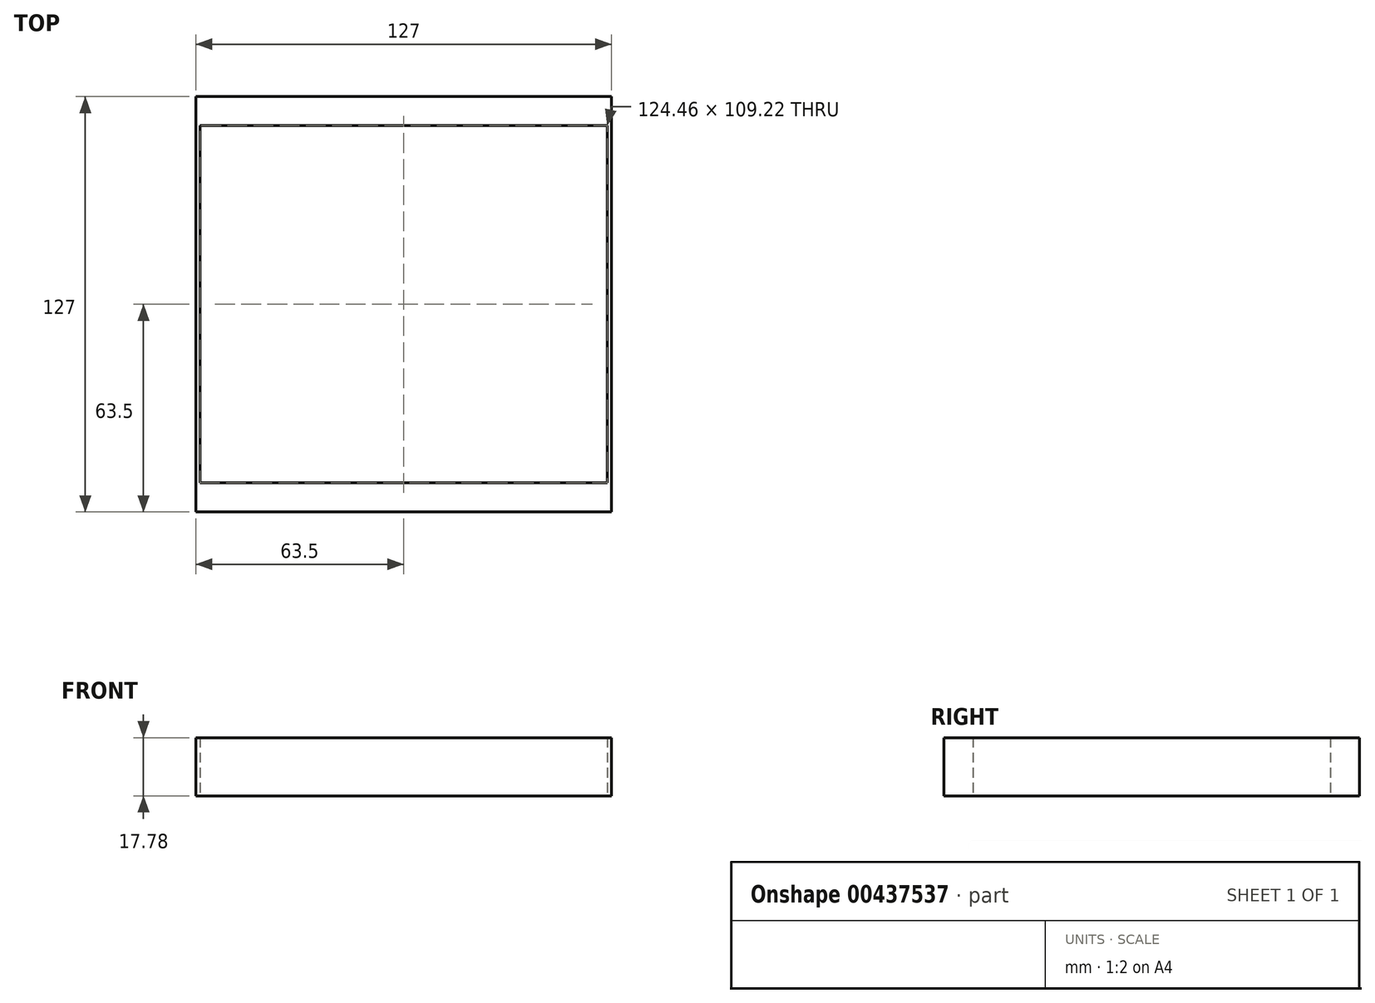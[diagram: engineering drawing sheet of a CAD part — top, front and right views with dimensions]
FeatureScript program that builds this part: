
annotation { "Feature Type Name" : "Feature", "Feature Type Description" : "" }
export const myFeature = defineFeature(function(context is Context, id is Id, definition is map)
    precondition{}
    {
        {
            var Q0;
            Q0=qCreatedBy(makeId("Top.planeOp"),FACE);
            var sketch = newSketch(context, id + "F0", { "sketchPlane" : qUnion([Q0])});
            skLineSegment(sketch, "E0.bottom", {"start": v(63.5, -63.5) * mm, "end": v(-63.5, -63.5) * mm});
            skLineSegment(sketch, "E0.top", {"start": v(63.5, 63.5) * mm, "end": v(-63.5, 63.5) * mm});
            skLineSegment(sketch, "E0.left", {"start": v(63.5, -63.5) * mm, "end": v(63.5, 63.5) * mm});
            skLineSegment(sketch, "E0.right", {"start": v(-63.5, -63.5) * mm, "end": v(-63.5, 63.5) * mm});
            skPoint(sketch, "E0.middle", {"position": v(0, 0) * mm});
            skLineSegment(sketch, "E1.bottom", {"start": v(47, -54.6) * mm, "end": v(-47, -54.61) * mm});
            skLineSegment(sketch, "E1.top", {"start": v(47, 54.6) * mm, "end": v(-47, 54.6) * mm});
            skLineSegment(sketch, "E1.left", {"start": v(47, -54.6) * mm, "end": v(47, 54.61) * mm});
            skLineSegment(sketch, "E1.right", {"start": v(-47, -54.61) * mm, "end": v(-47, 54.6) * mm});
            skLineSegment(sketch, "E2", {"start": v(-47, -54.61) * mm, "end": v(-63.5, -54.61) * mm});
            skLineSegment(sketch, "E3", {"start": v(47, -54.6) * mm, "end": v(63.5, -54.6) * mm});
            skLineSegment(sketch, "E4", {"start": v(-47, 54.6) * mm, "end": v(-63.5, 54.6) * mm});
            skLineSegment(sketch, "E5", {"start": v(47, 54.61) * mm, "end": v(63.5, 54.61) * mm});
            skLineSegment(sketch, "E6.bottom", {"start": v(-47, 54.6) * mm, "end": v(-48.26, 54.6) * mm});
            skLineSegment(sketch, "E6.top", {"start": v(-47, -54.61) * mm, "end": v(-48.26, -54.61) * mm});
            skLineSegment(sketch, "E6.left", {"start": v(-47, 54.6) * mm, "end": v(-46.99, -54.61) * mm});
            skLineSegment(sketch, "E6.right", {"start": v(-48.26, 54.6) * mm, "end": v(-48.26, -54.61) * mm});
            skLineSegment(sketch, "E7.bottom", {"start": v(-63.5, 54.6) * mm, "end": v(-62.23, 54.6) * mm});
            skLineSegment(sketch, "E7.top", {"start": v(-63.5, -54.61) * mm, "end": v(-62.23, -54.61) * mm});
            skLineSegment(sketch, "E7.left", {"start": v(-63.5, 54.6) * mm, "end": v(-63.5, -54.61) * mm});
            skLineSegment(sketch, "E7.right", {"start": v(-62.23, 54.6) * mm, "end": v(-62.23, -54.61) * mm});
            skLineSegment(sketch, "E8.bottom", {"start": v(47, 54.61) * mm, "end": v(48.26, 54.61) * mm});
            skLineSegment(sketch, "E8.top", {"start": v(47, -54.6) * mm, "end": v(48.26, -54.6) * mm});
            skLineSegment(sketch, "E8.left", {"start": v(47, 54.61) * mm, "end": v(47, -54.6) * mm});
            skLineSegment(sketch, "E8.right", {"start": v(48.26, 54.61) * mm, "end": v(48.26, -54.6) * mm});
            skLineSegment(sketch, "E9.bottom", {"start": v(63.5, 54.61) * mm, "end": v(62.23, 54.61) * mm});
            skLineSegment(sketch, "E9.top", {"start": v(63.5, -54.6) * mm, "end": v(62.23, -54.6) * mm});
            skLineSegment(sketch, "E9.left", {"start": v(63.5, 54.61) * mm, "end": v(63.5, -54.6) * mm});
            skLineSegment(sketch, "E9.right", {"start": v(62.23, 54.61) * mm, "end": v(62.23, -54.6) * mm});
            skLineSegment(sketch, "E10.bottom", {"start": v(53.34, 12.7) * mm, "end": v(58.42, 12.7) * mm});
            skLineSegment(sketch, "E10.top", {"start": v(53.34, -12.7) * mm, "end": v(58.42, -12.7) * mm});
            skLineSegment(sketch, "E10.left", {"start": v(53.34, 12.7) * mm, "end": v(53.34, -12.7) * mm});
            skLineSegment(sketch, "E10.right", {"start": v(58.42, 12.7) * mm, "end": v(58.42, -12.7) * mm});
            skPoint(sketch, "E10.middle", {"position": v(55.88, 0) * mm});
            skLineSegment(sketch, "E11.bottom", {"start": v(58.42, -27.94) * mm, "end": v(53.34, -27.94) * mm});
            skLineSegment(sketch, "E11.top", {"start": v(58.42, -53.34) * mm, "end": v(53.34, -53.34) * mm});
            skLineSegment(sketch, "E11.left", {"start": v(58.42, -27.94) * mm, "end": v(58.42, -53.34) * mm});
            skLineSegment(sketch, "E11.right", {"start": v(53.34, -27.94) * mm, "end": v(53.34, -53.34) * mm});
            skLineSegment(sketch, "E12", {"start": v(58.42, 40.64) * mm, "end": v(53.34, 40.64) * mm});
            skSolve(sketch);
        }
        {
            var Q0;
            Q0 = qSketchRegion(id + "F0", true);
            var Q1;
            Q1=makeQuery(id+"F0.imprint","IMPRINT",FACE,{"disambiguationData":[TD([[makeQuery(id+"F0.imprint","IMPRINT",EDGE,{"derivedFrom":sQuery(id+"F0.wireOp",EDGE,"E6.bottom")}),1.0]])]});
            var Q2;
            Q2=makeQuery(id+"F0.imprint","IMPRINT",FACE,{"disambiguationData":[TD([[makeQuery(id+"F0.imprint","IMPRINT",EDGE,{"derivedFrom":sQuery(id+"F0.wireOp",EDGE,"E8.bottom")}),-1.0]])]});
            extrude(context, id + "F1", {"entities" : qUnion([Q0, Q1, Q2]), "endBound" : BoundingType.SYMMETRIC, "depth" : 17.78 * mm});
        }
    });
